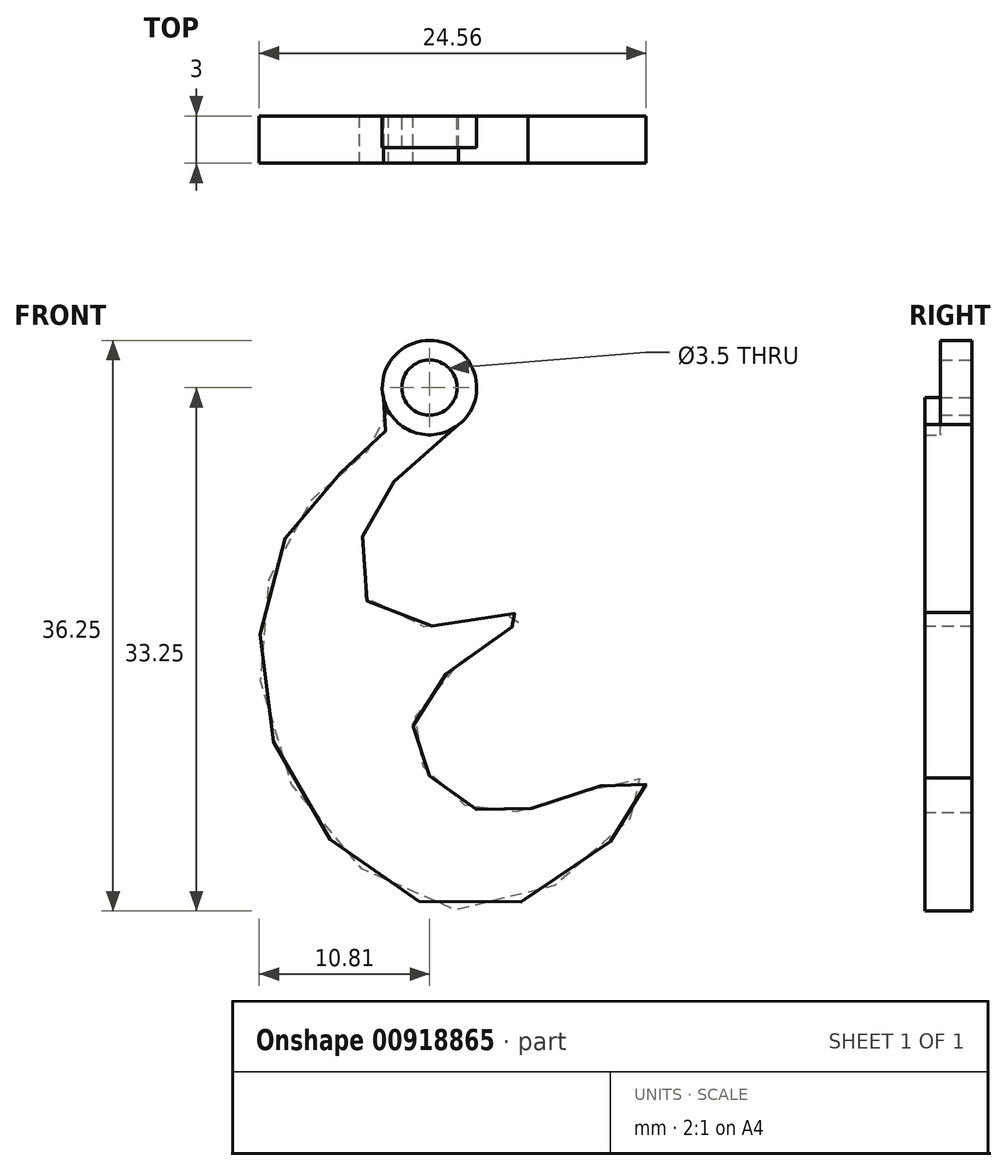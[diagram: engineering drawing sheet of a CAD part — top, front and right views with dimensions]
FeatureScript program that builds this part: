
annotation { "Feature Type Name" : "Feature", "Feature Type Description" : "" }
export const myFeature = defineFeature(function(context is Context, id is Id, definition is map)
    precondition{}
    {
        {
            var Q0;
            Q0=qCreatedBy(makeId("Front.planeOp"),FACE);
            var sketch = newSketch(context, id + "F0", { "sketchPlane" : qUnion([Q0])});
            skCircle(sketch, "E0", {"center": v(0, 0) * mm, "radius": 3 * mm});
            skFitSpline(sketch, "E1", {"points": [v(1.85, -2.36) * mm, v(-4.19, -9.17) * mm, v(-2.46, -14.86) * mm, v(6.23, -14.32) * mm, v(0.92, -18.31) * mm, v(-0.9, -23.03) * mm, v(2.77, -26.73) * mm, v(8.38, -26.15) * mm, v(13.7, -25.1) * mm, v(4.77, -33) * mm, v(-9.37, -23.94) * mm, v(-8.05, -7.8) * mm, v(-2.68, -2.46) * mm, v(-2.94, -0.62) * mm], "startDerivative": vector(-121.24, -99.73) * mm, "endDerivative": vector(0.23, 29.59) * mm});
            skCircle(sketch, "E2", {"center": v(0, 0) * mm, "radius": 1.75 * mm});
            skSolve(sketch);
        }
        {
            var Q0;
            {var subQ0=sQuery(id+"F0.wireOp",EDGE,"E1");Q0=makeQuery(id+"F0.imprint","IMPRINT",FACE,{"disambiguationData":[TD([[makeQuery(id+"F0.imprint","IMPRINT",EDGE,{"derivedFrom":subQ0}),-1.0]])]});}
            extrude(context, id + "F1", {"entities" : qUnion([Q0]), "depth" : 3 * mm, "offsetDistance" : 25 * mm});
        }
        {
            var Q0;
            Q0=makeQuery(id+"F0.imprint","IMPRINT",FACE,{"disambiguationData":[TD([[makeQuery(id+"F0.imprint","IMPRINT",EDGE,{"derivedFrom":sQuery(id+"F0.wireOp",EDGE,"E2")}),-1.0]])]});
            extrude(context, id + "F2", {"entities" : qUnion([Q0]), "operationType" : NewBodyOperationType.ADD, "depth" : 2 * mm, "offsetDistance" : 25 * mm});
        }
    });
